# Revit family: 5DMLH-NRG
name_source: partatom
category: Mechanical Equipment
units: mm (PartAtom-declared; Revit-internal decimal feet)

## family parameters
Always vertical = Yes
Cut with Voids When Loaded = No
OmniClass Number = 23.40.40.11.17
OmniClass Title = Refrigerated Cases
Part Type = Normal
Room Calculation Point = No
Round Connector Dimension = Use Radius
Shared = No
Work Plane-Based = Yes

## types (4) — shared parameters
24" Shelf = Yes
BOTTOM ELECTRICAL = Yes
BOTTOM REFRIGERATION PIPING = Yes
Certifications = NSF 7, UL471, CSA
DATE = 05/02/2016
DESIGNERS NAME = SHIDDRAMESH
DRAIN LINE CONNECTION = SANITARY CONNECTION
DRAIN LINE DIAMETER = 2"
DRAIN PIPE TYPE = PVC
DRAIN PIPING = Yes
DRIP PAN PLUMB TYPE = HARD
Default Elevation = 48"
Description = High Multi-Deck Merchandiser with Synerg-E™
EQUIPMENT DESCRIPTION = High Multi-Deck Merchandiser with Synerg-E™
EQUIPMENT MARK = 5DMLH-NRG
GLASS = Glass
Height = 82 5/8"
Item Description = High Multi-Deck Merchandiser with Synerg-E™
LF STD END = Yes
LIQUID LINE CONNECTION = LIQUID LINE CONNECTION
LIQUID LINE DIAMETER = 0"
LIQUID LINE RADIUS = 0"
Legend Number = 5DMLH-NRG
Manufacturer = HILL PHOENIX
Model = 5DMLH-NRG
PAINTED METAL UPPER SHELF = PAINTED SHELVES
REFRIGERATION PIPING = COPPER PIPE
RT STD END = Yes
SANITARY PIPE SIZE = 1"
STAINLESS STEEL = GALVANIZED STEEL
SUCTION LINE CONNECTION = SUCTION LINE CONNECTION
SUCTION LINE DIAMETER = 1"
SUCTION LINE RADIUS = 0"
TOP ELECTRICAL = Yes
TOP REFRIGERATION PIPING = Yes
URL = http://www.hillphoenix.com
Width = 42 3/4"

## per-type parameters (varying)
| type | DRAIN LINE | Length |
| 4' | 24" | 48" |
| 6' | 36" | 72" |
| 8' | 48" | 96" |
| 12' | 72" | 144" |

## geometry (parser evidence)
native form markers: Blend x13, Sweep x5
no freeform markers — native parametric forms only
